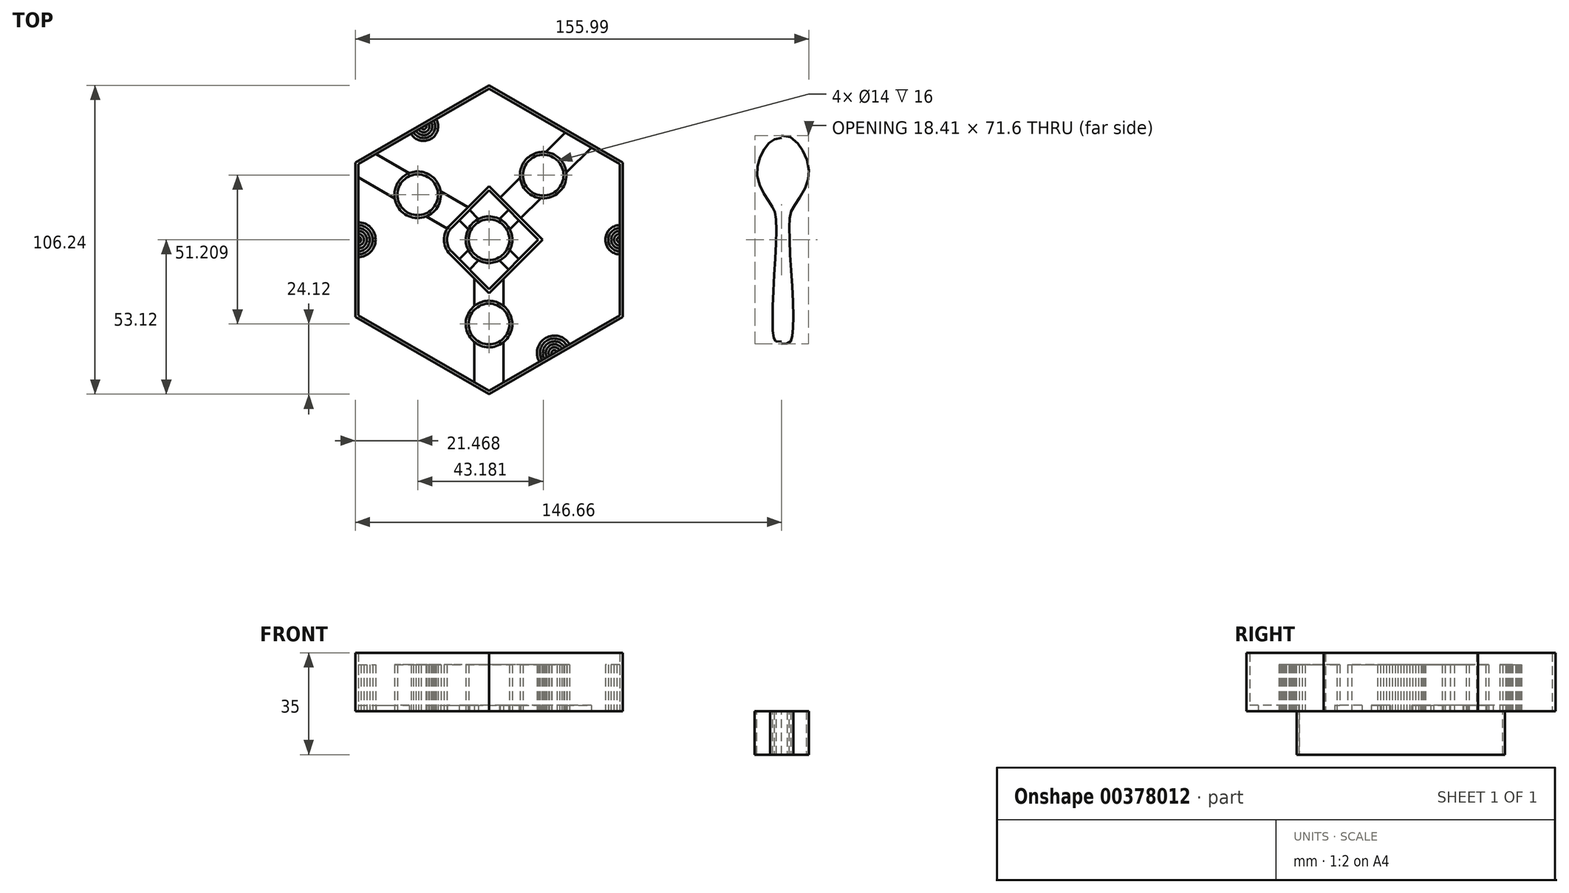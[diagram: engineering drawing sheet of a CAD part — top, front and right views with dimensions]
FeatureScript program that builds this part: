
annotation { "Feature Type Name" : "Feature", "Feature Type Description" : "" }
export const myFeature = defineFeature(function(context is Context, id is Id, definition is map)
    precondition{}
    {
        {
            var Q0;
            Q0=qCreatedBy(makeId("Top.planeOp"),FACE);
            var sketch = newSketch(context, id + "F0", { "sketchPlane" : qUnion([Q0])});
            skLineSegment(sketch, "E0", {"start": v(0, 0) * mm, "end": v(0, 35) * mm, "construction": true});
            skLineSegment(sketch, "E1", {"start": v(0, 0) * mm, "end": v(0, -35) * mm, "construction": true});
            skFitSpline(sketch, "E2", {"points": [v(0, 35) * mm, v(-5.38, 32.06) * mm, v(-8.44, 22.08) * mm, v(-3.94, 12.46) * mm, v(-2.02, 7.78) * mm, v(-2.87, -17.92) * mm, v(-2.58, -34.27) * mm, v(0, -35) * mm], "startDerivative": vector(-66.05, 0) * mm, "endDerivative": vector(72.92, 0) * mm});
            skFitSpline(sketch, "E3.MirrorCS", {"points": [v(0, 35) * mm, v(5.38, 32.06) * mm, v(8.44, 22.08) * mm, v(3.94, 12.46) * mm, v(2.02, 7.78) * mm, v(2.87, -17.92) * mm, v(2.58, -34.27) * mm, v(0, -35) * mm], "startDerivative": vector(66.05, 0) * mm, "endDerivative": vector(-72.92, 0) * mm});
            skFitSpline(sketch, "E4.0", {"points": [v(0, 35.8) * mm, v(-0.75, 35.8) * mm, v(-2.13, 35.62) * mm, v(-3.87, 34.8) * mm, v(-5.05, 33.75) * mm, v(-5.9, 32.73) * mm, v(-6.5, 31.88) * mm, v(-7.09, 30.94) * mm, v(-7.82, 29.6) * mm, v(-8.6, 27.74) * mm, v(-9.11, 25.73) * mm, v(-9.3, 24.06) * mm, v(-9.32, 22.8) * mm, v(-9.2, 21.51) * mm, v(-8.93, 20.26) * mm, v(-8.54, 19.05) * mm, v(-7.91, 17.48) * mm, v(-6.96, 15.65) * mm, v(-5.94, 14.02) * mm, v(-5.18, 12.87) * mm, v(-4.65, 12.09) * mm, v(-4.2, 11.41) * mm, v(-3.7, 10.61) * mm, v(-3.33, 9.9) * mm, v(-3.06, 9.05) * mm, v(-2.9, 8.3) * mm, v(-2.78, 7.4) * mm, v(-2.69, 6.3) * mm, v(-2.64, 5.04) * mm, v(-2.62, 3.17) * mm, v(-2.66, 0.5) * mm, v(-2.81, -3.08) * mm, v(-3.03, -6.94) * mm, v(-3.27, -10.95) * mm, v(-3.51, -15) * mm, v(-3.73, -18.98) * mm, v(-3.88, -22.77) * mm, v(-3.97, -26.25) * mm, v(-3.96, -28.8) * mm, v(-3.9, -30.59) * mm, v(-3.83, -31.78) * mm, v(-3.72, -32.82) * mm, v(-3.6, -33.56) * mm, v(-3.49, -34.07) * mm, v(-3.38, -34.42) * mm, v(-3.25, -34.74) * mm, v(-3.07, -35.05) * mm, v(-2.8, -35.35) * mm, v(-2.47, -35.56) * mm, v(-2.11, -35.69) * mm, v(-1.76, -35.75) * mm, v(-1.4, -35.79) * mm, v(-0.86, -35.8) * mm, v(-0.38, -35.8) * mm, v(0, -35.8) * mm]});
            skFitSpline(sketch, "E4.1", {"points": [v(0, 35.8) * mm, v(0.75, 35.8) * mm, v(2.13, 35.62) * mm, v(3.87, 34.8) * mm, v(5.05, 33.75) * mm, v(5.9, 32.73) * mm, v(6.5, 31.88) * mm, v(7.09, 30.94) * mm, v(7.82, 29.6) * mm, v(8.6, 27.74) * mm, v(9.11, 25.73) * mm, v(9.3, 24.06) * mm, v(9.32, 22.8) * mm, v(9.2, 21.51) * mm, v(8.93, 20.26) * mm, v(8.54, 19.05) * mm, v(7.91, 17.48) * mm, v(6.96, 15.65) * mm, v(5.94, 14.02) * mm, v(5.18, 12.87) * mm, v(4.65, 12.09) * mm, v(4.2, 11.41) * mm, v(3.7, 10.61) * mm, v(3.33, 9.9) * mm, v(3.06, 9.05) * mm, v(2.9, 8.3) * mm, v(2.78, 7.4) * mm, v(2.69, 6.3) * mm, v(2.64, 5.04) * mm, v(2.62, 3.17) * mm, v(2.66, 0.5) * mm, v(2.81, -3.08) * mm, v(3.03, -6.94) * mm, v(3.27, -10.95) * mm, v(3.51, -15) * mm, v(3.73, -18.98) * mm, v(3.88, -22.77) * mm, v(3.97, -26.25) * mm, v(3.96, -28.8) * mm, v(3.9, -30.59) * mm, v(3.83, -31.78) * mm, v(3.72, -32.82) * mm, v(3.6, -33.56) * mm, v(3.49, -34.07) * mm, v(3.38, -34.42) * mm, v(3.25, -34.74) * mm, v(3.07, -35.05) * mm, v(2.8, -35.35) * mm, v(2.47, -35.56) * mm, v(2.11, -35.69) * mm, v(1.76, -35.75) * mm, v(1.4, -35.79) * mm, v(0.86, -35.8) * mm, v(0.38, -35.8) * mm, v(0, -35.8) * mm]});
            skLineSegment(sketch, "E5", {"start": v(0, 0) * mm, "end": v(-100.66, 0) * mm, "construction": true});
            skCircle(sketch, "E6.cCircle", {"center": v(-100.66, 0) * mm, "radius": 45 * mm, "construction": true});
            skLineSegment(sketch, "E6.0", {"start": v(-145.66, 25.98) * mm, "end": v(-100.66, 51.96) * mm});
            skLineSegment(sketch, "E6.1", {"start": v(-100.66, 51.96) * mm, "end": v(-55.66, 25.98) * mm});
            skLineSegment(sketch, "E6.2", {"start": v(-55.66, 25.98) * mm, "end": v(-55.66, -25.98) * mm});
            skLineSegment(sketch, "E6.3", {"start": v(-55.66, -25.98) * mm, "end": v(-100.66, -51.96) * mm});
            skLineSegment(sketch, "E6.4", {"start": v(-100.66, -51.96) * mm, "end": v(-145.66, -25.98) * mm});
            skLineSegment(sketch, "E6.5", {"start": v(-145.66, -25.98) * mm, "end": v(-145.66, 25.98) * mm});
            skPoint(sketch, "E6.0.midPoint", {"position": v(-123.16, 38.97) * mm});
            skCircle(sketch, "E7", {"center": v(-100.66, 0) * mm, "radius": 7 * mm});
            skLineSegment(sketch, "E8", {"start": v(-100.66, 16.97) * mm, "end": v(-83.69, 0) * mm});
            skLineSegment(sketch, "E9", {"start": v(-83.69, 0) * mm, "end": v(-100.66, -16.97) * mm});
            skLineSegment(sketch, "E10", {"start": v(-100.66, -16.97) * mm, "end": v(-113.39, -4.24) * mm});
            skLineSegment(sketch, "E11", {"start": v(-113.39, 4.24) * mm, "end": v(-100.66, 16.97) * mm});
            skCircle(sketch, "E12", {"center": v(-100.66, 0) * mm, "radius": 29 * mm, "construction": true});
            skCircle(sketch, "E13", {"center": v(-125.2, 15.46) * mm, "radius": 7 * mm});
            skCircle(sketch, "E14", {"center": v(-82.01, 22.2) * mm, "radius": 7 * mm});
            skArc(sketch, "E15", {"start": v(-145.66, -3) * mm, "mid": v(-142.66, 0) * mm, "end": v(-145.66, 3) * mm});
            skArc(sketch, "E16", {"start": v(-145.66, -4) * mm, "mid": v(-141.66, 0) * mm, "end": v(-145.66, 4) * mm});
            skArc(sketch, "E17", {"start": v(-145.66, -5) * mm, "mid": v(-140.66, 0) * mm, "end": v(-145.66, 5) * mm});
            skArc(sketch, "E18", {"start": v(-145.66, -6) * mm, "mid": v(-139.66, 0) * mm, "end": v(-145.66, 6) * mm});
            skLineSegment(sketch, "E19", {"start": v(-145.66, -25.98) * mm, "end": v(-100.66, 0) * mm, "construction": true});
            skLineSegment(sketch, "E20", {"start": v(-145.66, 25.98) * mm, "end": v(-100.66, 0) * mm, "construction": true});
            skLineSegment(sketch, "E21", {"start": v(-100.66, 51.96) * mm, "end": v(-100.66, 0) * mm, "construction": true});
            skLineSegment(sketch, "E22", {"start": v(-100.66, 0) * mm, "end": v(-55.66, 25.98) * mm, "construction": true});
            skLineSegment(sketch, "E23", {"start": v(-100.66, 0) * mm, "end": v(-55.66, -25.98) * mm, "construction": true});
            skLineSegment(sketch, "E24", {"start": v(-100.66, 0) * mm, "end": v(-100.66, -51.96) * mm, "construction": true});
            skLineSegment(sketch, "E25.0", {"start": v(-146.66, -26.56) * mm, "end": v(-146.66, 26.56) * mm});
            skLineSegment(sketch, "E25.1", {"start": v(-100.66, 53.12) * mm, "end": v(-54.66, 26.56) * mm});
            skLineSegment(sketch, "E25.2", {"start": v(-54.66, 26.56) * mm, "end": v(-54.66, -26.56) * mm});
            skLineSegment(sketch, "E25.3", {"start": v(-146.66, 26.56) * mm, "end": v(-100.66, 53.12) * mm});
            skLineSegment(sketch, "E25.4", {"start": v(-54.66, -26.56) * mm, "end": v(-100.66, -53.12) * mm});
            skLineSegment(sketch, "E25.5", {"start": v(-100.66, -53.12) * mm, "end": v(-146.66, -26.56) * mm});
            skCircle(sketch, "E26", {"center": v(-100.66, -29) * mm, "radius": 7 * mm});
            skArc(sketch, "E27", {"start": v(-145.66, -2) * mm, "mid": v(-143.66, 0) * mm, "end": v(-145.66, 2) * mm});
            skArc(sketch, "E28", {"start": v(-145.66, -1) * mm, "mid": v(-144.66, 0) * mm, "end": v(-145.66, 1) * mm});
            skArc(sketch, "E29.MirrorCS", {"start": v(-122.3, 39.47) * mm, "mid": v(-122.66, 38.1) * mm, "end": v(-124.03, 38.47) * mm});
            skArc(sketch, "E30.MirrorCS", {"start": v(-121.43, 39.97) * mm, "mid": v(-122.16, 37.24) * mm, "end": v(-124.9, 37.97) * mm});
            skArc(sketch, "E31.MirrorCS", {"start": v(-120.56, 40.47) * mm, "mid": v(-121.66, 36.37) * mm, "end": v(-125.76, 37.47) * mm});
            skArc(sketch, "E32.MirrorCS", {"start": v(-119.7, 40.97) * mm, "mid": v(-121.16, 35.5) * mm, "end": v(-126.62, 36.97) * mm});
            skArc(sketch, "E33.MirrorCS", {"start": v(-118.83, 41.47) * mm, "mid": v(-120.66, 34.64) * mm, "end": v(-127.49, 36.47) * mm});
            skArc(sketch, "E34.MirrorCS", {"start": v(-117.96, 41.97) * mm, "mid": v(-120.16, 33.77) * mm, "end": v(-128.36, 35.97) * mm});
            skArc(sketch, "E35.MirrorCS", {"start": v(-77.3, -38.47) * mm, "mid": v(-78.66, -38.1) * mm, "end": v(-79.03, -39.47) * mm});
            skArc(sketch, "E36.MirrorCS", {"start": v(-75.56, -37.47) * mm, "mid": v(-79.66, -36.37) * mm, "end": v(-80.76, -40.47) * mm});
            skArc(sketch, "E37.MirrorCS", {"start": v(-76.43, -37.97) * mm, "mid": v(-79.16, -37.24) * mm, "end": v(-79.9, -39.97) * mm});
            skArc(sketch, "E38.MirrorCS", {"start": v(-74.7, -36.97) * mm, "mid": v(-80.16, -35.5) * mm, "end": v(-81.62, -40.97) * mm});
            skArc(sketch, "E39.MirrorCS", {"start": v(-73.83, -36.47) * mm, "mid": v(-80.66, -34.64) * mm, "end": v(-82.49, -41.47) * mm});
            skArc(sketch, "E40.MirrorCS", {"start": v(-72.96, -35.97) * mm, "mid": v(-81.16, -33.77) * mm, "end": v(-83.36, -41.97) * mm});
            skArc(sketch, "E41.MirrorCS", {"start": v(-55.66, -1) * mm, "mid": v(-56.66, 0) * mm, "end": v(-55.66, 1) * mm});
            skArc(sketch, "E42.MirrorCS", {"start": v(-55.66, -2) * mm, "mid": v(-57.66, 0) * mm, "end": v(-55.66, 2) * mm});
            skArc(sketch, "E43.MirrorCS", {"start": v(-55.66, -3) * mm, "mid": v(-58.66, 0) * mm, "end": v(-55.66, 3) * mm});
            skArc(sketch, "E44.MirrorCS", {"start": v(-55.66, -4) * mm, "mid": v(-59.66, 0) * mm, "end": v(-55.66, 4) * mm});
            skArc(sketch, "E45.MirrorCS", {"start": v(-55.66, -5) * mm, "mid": v(-60.66, 0) * mm, "end": v(-55.66, 5) * mm});
            skArc(sketch, "E46.MirrorCS", {"start": v(-55.66, -6) * mm, "mid": v(-61.66, 0) * mm, "end": v(-55.66, 6) * mm});
            skCircle(sketch, "E47.0", {"center": v(-125.2, 15.46) * mm, "radius": 8 * mm});
            skCircle(sketch, "E48.0", {"center": v(-82.01, 22.2) * mm, "radius": 8 * mm});
            skCircle(sketch, "E49.0", {"center": v(-100.66, -29) * mm, "radius": 8 * mm});
            skLineSegment(sketch, "E50.0", {"start": v(-114.1, 4.95) * mm, "end": v(-100.66, 18.38) * mm});
            skLineSegment(sketch, "E50.1", {"start": v(-100.66, -18.38) * mm, "end": v(-114.1, -4.95) * mm});
            skLineSegment(sketch, "E50.2", {"start": v(-82.27, 0) * mm, "end": v(-100.66, -18.38) * mm});
            skLineSegment(sketch, "E50.3", {"start": v(-100.66, 18.38) * mm, "end": v(-82.27, 0) * mm});
            skPoint(sketch, "E51.visualSharp", {"position": v(-117.63, 0) * mm});
            skArc(sketch, "E51.filletArc", {"start": v(-113.39, 4.24) * mm, "mid": v(-115.14, 0) * mm, "end": v(-113.39, -4.24) * mm});
            skPoint(sketch, "E52.visualSharp", {"position": v(-119.04, 0) * mm});
            skArc(sketch, "E52.filletArc", {"start": v(-114.1, 4.95) * mm, "mid": v(-116.14, 0) * mm, "end": v(-114.1, -4.95) * mm});
            skLineSegment(sketch, "E53", {"start": v(-69.97, 34.25) * mm, "end": v(-93.25, 10.97) * mm, "construction": true});
            skLineSegment(sketch, "E54", {"start": v(-144.53, 26.63) * mm, "end": v(-111.5, 7.55) * mm, "construction": true});
            skLineSegment(sketch, "E55.0", {"start": v(-74.46, 36.83) * mm, "end": v(-81.13, 30.16) * mm});
            skLineSegment(sketch, "E56.0", {"start": v(-65.5, 31.66) * mm, "end": v(-74.06, 23.09) * mm});
            skLineSegment(sketch, "E57.0", {"start": v(-105.66, -13.38) * mm, "end": v(-105.66, -22.76) * mm});
            skLineSegment(sketch, "E58.0", {"start": v(-95.66, -13.38) * mm, "end": v(-95.66, -22.76) * mm});
            skLineSegment(sketch, "E59.0", {"start": v(-145.66, 21.5) * mm, "end": v(-133.1, 14.26) * mm});
            skLineSegment(sketch, "E60.0", {"start": v(-139.53, 29.52) * mm, "end": v(-128.1, 22.92) * mm});
            skLineSegment(sketch, "E61.trimOffspring", {"start": v(-105.66, -35.24) * mm, "end": v(-105.66, -49.07) * mm});
            skLineSegment(sketch, "E62.trimOffspring", {"start": v(-95.66, -35.24) * mm, "end": v(-95.66, -49.07) * mm});
            skLineSegment(sketch, "E63.trimOffspring", {"start": v(-117.28, 16.67) * mm, "end": v(-107.83, 11.21) * mm});
            skLineSegment(sketch, "E64.trimOffspring", {"start": v(-122.28, 8.01) * mm, "end": v(-114, 3.22) * mm});
            skLineSegment(sketch, "E65.trimOffspring", {"start": v(-89.96, 21.33) * mm, "end": v(-96.78, 14.5) * mm});
            skLineSegment(sketch, "E66.trimOffspring", {"start": v(-82.9, 14.26) * mm, "end": v(-89.71, 7.44) * mm});
            skCircle(sketch, "E67.0", {"center": v(-100.66, 0) * mm, "radius": 8 * mm});
            skLineSegment(sketch, "E68", {"start": v(-92.17, 8.49) * mm, "end": v(-109.14, -8.49) * mm, "construction": true});
            skLineSegment(sketch, "E69", {"start": v(-109.14, 8.49) * mm, "end": v(-92.17, -8.49) * mm, "construction": true});
            skLineSegment(sketch, "E70.0", {"start": v(-93.94, 10.25) * mm, "end": v(-97.05, 7.14) * mm});
            skLineSegment(sketch, "E71.0", {"start": v(-90.4, 6.72) * mm, "end": v(-93.52, 3.6) * mm});
            skLineSegment(sketch, "E72.0", {"start": v(-110.91, 6.72) * mm, "end": v(-107.8, 3.6) * mm});
            skLineSegment(sketch, "E73.0", {"start": v(-107.38, 10.25) * mm, "end": v(-104.27, 7.14) * mm});
            skLineSegment(sketch, "E74.trimOffspring", {"start": v(-93.52, -3.6) * mm, "end": v(-90.4, -6.72) * mm});
            skLineSegment(sketch, "E75.trimOffspring", {"start": v(-107.8, -3.6) * mm, "end": v(-110.91, -6.72) * mm});
            skLineSegment(sketch, "E76.trimOffspring", {"start": v(-97.05, -7.14) * mm, "end": v(-93.94, -10.25) * mm});
            skLineSegment(sketch, "E77.trimOffspring", {"start": v(-104.27, -7.14) * mm, "end": v(-107.38, -10.25) * mm});
            skSolve(sketch);
        }
        {
            var Q0;
            Q0=makeQuery(id+"F0.imprint","IMPRINT",FACE,{"disambiguationData":[TD([[makeQuery(id+"F0.imprint","IMPRINT",EDGE,{"derivedFrom":sQuery(id+"F0.wireOp",EDGE,"E4.0")}),1.0]])]});
            extrude(context, id + "F1", {"entities" : qUnion([Q0]), "oppositeDirection" : true, "depth" : 15 * mm});
        }
        {
            var Q0;
            {var subQ63=sQuery(id+"F0.wireOp",EDGE,"E6.1");Q0=makeQuery(id+"F0.imprint","IMPRINT",FACE,{"disambiguationData":[TD([[makeQuery(id+"F0.imprint","IMPRINT",EDGE,{"derivedFrom":subQ63}),1.0]])]});}
            extrude(context, id + "F2", {"entities" : qUnion([Q0]), "depth" : 20 * mm});
        }
        {
            var Q0;
            {var subQ0=sQuery(id+"F0.wireOp",EDGE,"E33.MirrorCS");Q0=makeQuery(id+"F0.imprint","IMPRINT",FACE,{"disambiguationData":[TD([[makeQuery(id+"F0.imprint","IMPRINT",EDGE,{"derivedFrom":subQ0}),1.0]])]});}
            var Q1;
            {var subQ0=sQuery(id+"F0.wireOp",EDGE,"E31.MirrorCS");Q1=makeQuery(id+"F0.imprint","IMPRINT",FACE,{"disambiguationData":[TD([[makeQuery(id+"F0.imprint","IMPRINT",EDGE,{"derivedFrom":subQ0}),1.0]])]});}
            var Q2;
            {var subQ0=sQuery(id+"F0.wireOp",EDGE,"E29.MirrorCS");Q2=makeQuery(id+"F0.imprint","IMPRINT",FACE,{"disambiguationData":[TD([[makeQuery(id+"F0.imprint","IMPRINT",EDGE,{"derivedFrom":subQ0}),1.0]])]});}
            var Q3;
            {var subQ0=sQuery(id+"F0.wireOp",EDGE,"E17");Q3=makeQuery(id+"F0.imprint","IMPRINT",FACE,{"disambiguationData":[TD([[makeQuery(id+"F0.imprint","IMPRINT",EDGE,{"derivedFrom":subQ0}),-1.0]])]});}
            var Q4;
            {var subQ0=sQuery(id+"F0.wireOp",EDGE,"E15");Q4=makeQuery(id+"F0.imprint","IMPRINT",FACE,{"disambiguationData":[TD([[makeQuery(id+"F0.imprint","IMPRINT",EDGE,{"derivedFrom":subQ0}),-1.0]])]});}
            var Q5;
            {var subQ0=sQuery(id+"F0.wireOp",EDGE,"E27");Q5=makeQuery(id+"F0.imprint","IMPRINT",FACE,{"disambiguationData":[TD([[makeQuery(id+"F0.imprint","IMPRINT",EDGE,{"derivedFrom":subQ0}),1.0]])]});}
            var Q6;
            {var subQ0=sQuery(id+"F0.wireOp",EDGE,"E39.MirrorCS");Q6=makeQuery(id+"F0.imprint","IMPRINT",FACE,{"disambiguationData":[TD([[makeQuery(id+"F0.imprint","IMPRINT",EDGE,{"derivedFrom":subQ0}),-1.0]])]});}
            var Q7;
            {var subQ0=sQuery(id+"F0.wireOp",EDGE,"E36.MirrorCS");Q7=makeQuery(id+"F0.imprint","IMPRINT",FACE,{"disambiguationData":[TD([[makeQuery(id+"F0.imprint","IMPRINT",EDGE,{"derivedFrom":subQ0}),-1.0]])]});}
            var Q8;
            {var subQ0=sQuery(id+"F0.wireOp",EDGE,"E35.MirrorCS");Q8=makeQuery(id+"F0.imprint","IMPRINT",FACE,{"disambiguationData":[TD([[makeQuery(id+"F0.imprint","IMPRINT",EDGE,{"derivedFrom":subQ0}),-1.0]])]});}
            var Q9;
            {var subQ0=sQuery(id+"F0.wireOp",EDGE,"E45.MirrorCS");Q9=makeQuery(id+"F0.imprint","IMPRINT",FACE,{"disambiguationData":[TD([[makeQuery(id+"F0.imprint","IMPRINT",EDGE,{"derivedFrom":subQ0}),1.0]])]});}
            var Q10;
            {var subQ0=sQuery(id+"F0.wireOp",EDGE,"E43.MirrorCS");Q10=makeQuery(id+"F0.imprint","IMPRINT",FACE,{"disambiguationData":[TD([[makeQuery(id+"F0.imprint","IMPRINT",EDGE,{"derivedFrom":subQ0}),1.0]])]});}
            var Q11;
            {var subQ0=sQuery(id+"F0.wireOp",EDGE,"E41.MirrorCS");Q11=makeQuery(id+"F0.imprint","IMPRINT",FACE,{"disambiguationData":[TD([[makeQuery(id+"F0.imprint","IMPRINT",EDGE,{"derivedFrom":subQ0}),1.0]])]});}
            var Q12;
            Q12=makeQuery(id+"F0.imprint","IMPRINT",FACE,{"disambiguationData":[TD([[makeQuery(id+"F0.imprint","IMPRINT",EDGE,{"derivedFrom":sQuery(id+"F0.wireOp",EDGE,"E13")}),-1.0]])]});
            var Q13;
            Q13=makeQuery(id+"F0.imprint","IMPRINT",FACE,{"disambiguationData":[TD([[makeQuery(id+"F0.imprint","IMPRINT",EDGE,{"derivedFrom":sQuery(id+"F0.wireOp",EDGE,"E14")}),-1.0]])]});
            var Q14;
            Q14=makeQuery(id+"F0.imprint","IMPRINT",FACE,{"disambiguationData":[TD([[makeQuery(id+"F0.imprint","IMPRINT",EDGE,{"derivedFrom":sQuery(id+"F0.wireOp",EDGE,"E8")}),1.0]])]});
            var Q15;
            Q15=makeQuery(id+"F0.imprint","IMPRINT",FACE,{"disambiguationData":[TD([[makeQuery(id+"F0.imprint","IMPRINT",EDGE,{"derivedFrom":sQuery(id+"F0.wireOp",EDGE,"E26")}),-1.0]])]});
            var Q16;
            Q16=makeQuery(id+"F0.imprint","IMPRINT",FACE,{"disambiguationData":[TD([[makeQuery(id+"F0.imprint","IMPRINT",EDGE,{"derivedFrom":sQuery(id+"F0.wireOp",EDGE,"E7")}),-1.0]])]});
            extrude(context, id + "F3", {"entities" : qUnion([Q0, Q1, Q2, Q3, Q4, Q5, Q6, Q7, Q8, Q9, Q10, Q11, Q12, Q13, Q14, Q15, Q16]), "operationType" : NewBodyOperationType.ADD, "depth" : 16 * mm});
        }
        {
            var Q0;
            {var subQ0=sQuery(id+"F0.wireOp",EDGE,"E59.0");Q0=makeQuery(id+"F0.imprint","IMPRINT",FACE,{"disambiguationData":[TD([[makeQuery(id+"F0.imprint","IMPRINT",EDGE,{"derivedFrom":subQ0}),1.0]])]});}
            var Q1;
            {var subQ3=sQuery(id+"F0.wireOp",EDGE,"E63.trimOffspring");Q1=makeQuery(id+"F0.imprint","IMPRINT",FACE,{"disambiguationData":[TD([[makeQuery(id+"F0.imprint","IMPRINT",EDGE,{"derivedFrom":subQ3}),-1.0]])]});}
            var Q2;
            {var subQ0=sQuery(id+"F0.wireOp",EDGE,"E65.trimOffspring");Q2=makeQuery(id+"F0.imprint","IMPRINT",FACE,{"disambiguationData":[TD([[makeQuery(id+"F0.imprint","IMPRINT",EDGE,{"derivedFrom":subQ0}),1.0]])]});}
            var Q3;
            {var subQ0=sQuery(id+"F0.wireOp",EDGE,"E55.0");Q3=makeQuery(id+"F0.imprint","IMPRINT",FACE,{"disambiguationData":[TD([[makeQuery(id+"F0.imprint","IMPRINT",EDGE,{"derivedFrom":subQ0}),1.0]])]});}
            var Q4;
            {var subQ0=sQuery(id+"F0.wireOp",EDGE,"E57.0");Q4=makeQuery(id+"F0.imprint","IMPRINT",FACE,{"disambiguationData":[TD([[makeQuery(id+"F0.imprint","IMPRINT",EDGE,{"derivedFrom":subQ0}),1.0]])]});}
            var Q5;
            {var subQ0=sQuery(id+"F0.wireOp",EDGE,"E61.trimOffspring");Q5=makeQuery(id+"F0.imprint","IMPRINT",FACE,{"disambiguationData":[TD([[makeQuery(id+"F0.imprint","IMPRINT",EDGE,{"derivedFrom":subQ0}),1.0]])]});}
            var Q6;
            {var subQ0=sQuery(id+"F0.wireOp",EDGE,"E75.trimOffspring");Q6=makeQuery(id+"F0.imprint","IMPRINT",FACE,{"disambiguationData":[TD([[makeQuery(id+"F0.imprint","IMPRINT",EDGE,{"derivedFrom":subQ0}),1.0]])]});}
            var Q7;
            {var subQ0=sQuery(id+"F0.wireOp",EDGE,"E72.0");Q7=makeQuery(id+"F0.imprint","IMPRINT",FACE,{"disambiguationData":[TD([[makeQuery(id+"F0.imprint","IMPRINT",EDGE,{"derivedFrom":subQ0}),1.0]])]});}
            var Q8;
            {var subQ0=sQuery(id+"F0.wireOp",EDGE,"E70.0");Q8=makeQuery(id+"F0.imprint","IMPRINT",FACE,{"disambiguationData":[TD([[makeQuery(id+"F0.imprint","IMPRINT",EDGE,{"derivedFrom":subQ0}),1.0]])]});}
            var Q9;
            {var subQ0=sQuery(id+"F0.wireOp",EDGE,"E74.trimOffspring");Q9=makeQuery(id+"F0.imprint","IMPRINT",FACE,{"disambiguationData":[TD([[makeQuery(id+"F0.imprint","IMPRINT",EDGE,{"derivedFrom":subQ0}),-1.0]])]});}
            extrude(context, id + "F4", {"entities" : qUnion([Q0, Q1, Q2, Q3, Q4, Q5, Q6, Q7, Q8, Q9]), "operationType" : NewBodyOperationType.ADD, "depth" : 2 * mm});
        }
    });
